# Revit family: Sanitary_Toilet-Cisterns_Sanindusa_Switch-Built-in-Cistern-for-Low-Level-Wc
name_source: partatom
category: Plumbing Fixtures
revit_build: Autodesk Revit 2018 (Build: 20170223_1515(x64)
units: mm (PartAtom-declared; Revit-internal decimal feet)

## family parameters
Always vertical = Yes
Cut with Voids When Loaded = No
Host = Wall
OmniClass Number = 23.45.00.00
OmniClass Title = Sanitary, Laundry, and Cleaning Equipment
Part Type = Normal
Room Calculation Point = No
Round Connector Dimension = Use Diameter
Shared = No

## types (1)
- Sanindusa
    AssetType = Fixed
    CisternCapacity = 6 Lts
    CisternColor = white
    CisternHeight = HighLevel
    CisternMaterial = ABS
    CodePerformance = EN 14055:2010 CL 1 - 9 - NL II - VR I
    Constituents = General content (material included): Angle valve for connection to the water supply, DN 15 (1/2"); Connection pipe to the toilet Ø 45 x 380 mm; Ø 45 adapter piece. Other parts necessary to fix and connect the product.Compatible plates (not included): 40003 - Orange 3|6L mechanism plate, 40013 - Plan 3|6L mechanism plate, 40023 - Easy 3|6L mechanism plate, 40033 - Moon 3|6L mechanism plate, 40043 - Square mechanism plate.
    Cost = 0 $
    Description = Switch built-in cistern for low level wc with 3|6L mechanism
    Edition number = 1
    Element Type = CISTERN: A water storage unit attached to a sanitary terminal that is fitted with a device, operated automatically or by the user, that discharges water to cleanse a water closet (toilet) pan, urinal or slop hopper. (BS6100 330 5008)
    Features = Concealed flushing cistern for a floor mounted toilet bowl. Installation height depends on the selected toilet bowl. Flushing cistern depth: 120 mm. For frontal activation. Used for mounting a dual flush flushing plate. The flushing cistern is insulated against condensation. Silent HDV-filling valve. Flushing cistern volume: 6 litres. Mounting for dual flush. Large flush: 6 L. Small flush: 3 L. Connection to the water supply: at the top middle/right side.
    FlushRate = Lowerbound:3 Lts
Upperbound:6 Lts
    FlushType = push
    Installation Instructions = https://www.tec.sanindusa.pt
    IsAutomaticFlush = FALSE
    IsSingleFlush = FALSE
    Manufacturer = www.sanindusa.pt
    ManufacturerName = Sanindusa
    ManufacturerURL = www.tec.sanindusa.pt
    Material = Flushing cistern is made from ABS material
    ModelNumber = 40133
    ModelReference = Switch
    Name = Switch built-in cistern for low level wc
    NominalHeight = 806 mm
    NominalLength = 510 mm  [stored 1.67323 ft]
    NominalWidth = 120 mm  [stored 0.393701 ft]
    Pre-defined type (IFC) = CISTERN
    Product Guid = c51be983-5501-49ad-abe9-cde046a925f7
    Product data url = https://bimobject.com
    Size = 51x12x81
    Type (IFC) = IfcSanitaryTerminalType
    URL = www.tec.sanindusa.pt
    Uniclass2015Code = Pr_40_20_93_89
    Uniclass2015Title = WC cisterns
    Uniclass2015Version = Products v1.6
    Version = 2
    WarrantyDescription = https://www.tec.sanindusa.pt
    WarrantyDurationParts = 5
    WarrantyDurationUnit = year
    WarrantyStartDate = 1900-12-31T23:59:59
    Weight = 5.40 kg
    X = 355 mm  [stored 1.1647 ft]

note: [stored X ft] marks values corroborated as IEEE doubles in the binary element streams (Revit-internal decimal feet)

## geometry (parser evidence)
native form markers: Sweep x5
no freeform markers — native parametric forms only
